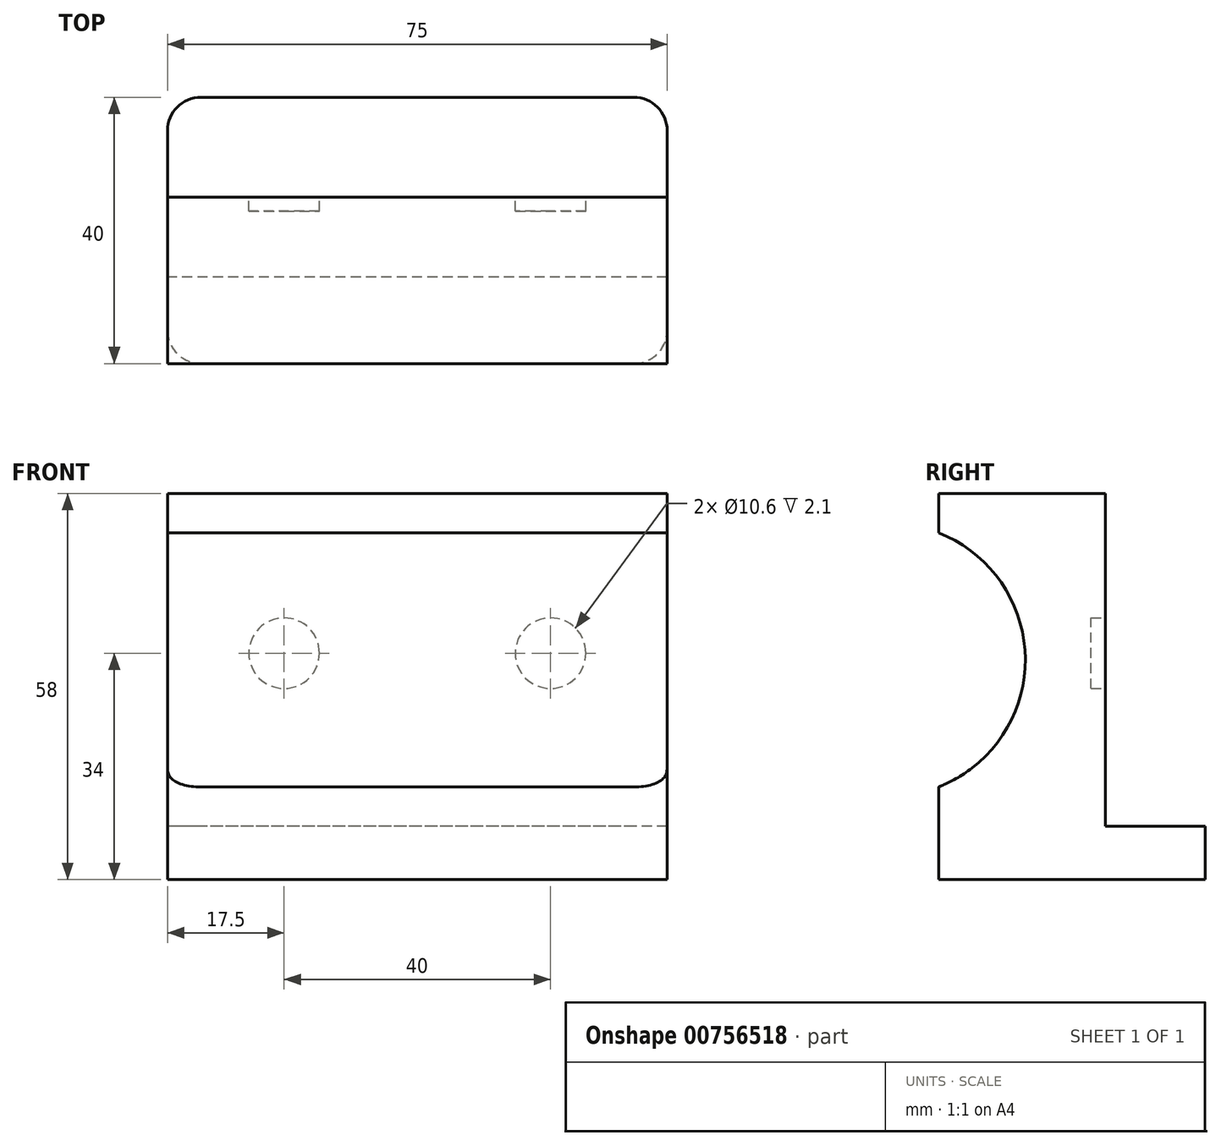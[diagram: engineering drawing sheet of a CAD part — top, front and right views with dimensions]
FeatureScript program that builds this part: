
annotation { "Feature Type Name" : "Feature", "Feature Type Description" : "" }
export const myFeature = defineFeature(function(context is Context, id is Id, definition is map)
    precondition{}
    {
        {
            var Q0;
            Q0=qCreatedBy(makeId("Top.planeOp"),FACE);
            var sketch = newSketch(context, id + "F0", { "sketchPlane" : qUnion([Q0])});
            skLineSegment(sketch, "E0.bottom", {"start": v(37.5, -12.5) * mm, "end": v(-37.5, -12.5) * mm});
            skLineSegment(sketch, "E0.top", {"start": v(37.5, 12.5) * mm, "end": v(-37.5, 12.5) * mm});
            skLineSegment(sketch, "E0.left", {"start": v(37.5, -12.5) * mm, "end": v(37.5, 12.5) * mm});
            skLineSegment(sketch, "E0.right", {"start": v(-37.5, -12.5) * mm, "end": v(-37.5, 12.5) * mm});
            skPoint(sketch, "E0.middle", {"position": v(0, 0) * mm});
            skSolve(sketch);
        }
        {
            var Q0;
            Q0 = qSketchRegion(id + "F0", true);
            extrude(context, id + "F1", {"entities" : qUnion([Q0]), "depth" : 50 * mm, "offsetDistance" : 25 * mm});
        }
        {
            var Q0;
            Q0=qCreatedBy(makeId("Right.planeOp"),FACE);
            var sketch = newSketch(context, id + "F2", { "sketchPlane" : qUnion([Q0])});
            skLineSegment(sketch, "E1", {"start": v(0, 0) * mm, "end": v(-20, 0) * mm});
            skLineSegment(sketch, "E2", {"start": v(-20, 0) * mm, "end": v(-20, 25) * mm});
            skCircle(sketch, "E3", {"center": v(-20, 25) * mm, "radius": 20.5 * mm});
            skSolve(sketch);
        }
        {
            var Q0;
            Q0 = qSketchRegion(id + "F2", true);
            extrude(context, id + "F3", {"entities" : qUnion([Q0]), "endBound" : BoundingType.SYMMETRIC, "depth" : 100 * mm, "offsetDistance" : 25 * mm});
        }
        {
            var Q0;
            Q0=makeQuery(id+"F3.opExtrude","SWEPT_BODY",BODY,{"disambiguationData":[OSD([sQuery(id+"F2.wireOp",EDGE,"E3")])]});
            var Q1;
            Q1=makeQuery(id+"F1.opExtrude","SWEPT_BODY",BODY,{"disambiguationData":[OSD([sQuery(id+"F0.wireOp",EDGE,"E0.bottom"),sQuery(id+"F0.wireOp",EDGE,"E0.top"),sQuery(id+"F0.wireOp",EDGE,"E0.left"),sQuery(id+"F0.wireOp",EDGE,"E0.right")])]});
            booleanBodies(context, id + "F4", {"operationType" : BooleanOperationType.SUBTRACTION, "tools" : qUnion([Q0]), "targets" : qUnion([Q1])});
        }
        {
            var Q0;
            Q0=qCreatedBy(makeId("Top.planeOp"),FACE);
            var sketch = newSketch(context, id + "F5", { "sketchPlane" : qUnion([Q0])});
            skLineSegment(sketch, "E4.bottom", {"start": v(37.5, -20) * mm, "end": v(-37.5, -20) * mm});
            skLineSegment(sketch, "E4.top", {"start": v(37.5, 20) * mm, "end": v(-37.5, 20) * mm});
            skLineSegment(sketch, "E4.left", {"start": v(37.5, -20) * mm, "end": v(37.5, 20) * mm});
            skLineSegment(sketch, "E4.right", {"start": v(-37.5, -20) * mm, "end": v(-37.5, 20) * mm});
            skPoint(sketch, "E4.middle", {"position": v(0, 0) * mm});
            skSolve(sketch);
        }
        {
            var Q0;
            Q0 = qSketchRegion(id + "F5", true);
            extrude(context, id + "F6", {"entities" : qUnion([Q0]), "depth" : 8 * mm, "offsetDistance" : 25 * mm});
        }
        {
            var Q0;
            Q0=makeQuery(id+"F6.opExtrude","SWEPT_BODY",BODY,{"disambiguationData":[OSD([sQuery(id+"F5.wireOp",EDGE,"E4.bottom"),sQuery(id+"F5.wireOp",EDGE,"E4.top"),sQuery(id+"F5.wireOp",EDGE,"E4.left"),sQuery(id+"F5.wireOp",EDGE,"E4.right")])]});
            transform(context, id + "F7", {"entities" : qUnion([Q0]), "transformType" : TransformType.TRANSLATION_3D, "dx" : 0 * mm, "dy" : 7.5 * mm, "dz" : -8 * mm, "makeCopy" : false});
        }
        {
            var Q0;
            Q0=makeQuery(id+"F6.opExtrude","SWEPT_BODY",BODY,{"disambiguationData":[OSD([sQuery(id+"F5.wireOp",EDGE,"E4.bottom"),sQuery(id+"F5.wireOp",EDGE,"E4.top"),sQuery(id+"F5.wireOp",EDGE,"E4.left"),sQuery(id+"F5.wireOp",EDGE,"E4.right")])]});
            var Q1;
            Q1=makeQuery(id+"F1.opExtrude","SWEPT_BODY",BODY,{"disambiguationData":[OSD([sQuery(id+"F0.wireOp",EDGE,"E0.bottom"),sQuery(id+"F0.wireOp",EDGE,"E0.top"),sQuery(id+"F0.wireOp",EDGE,"E0.left"),sQuery(id+"F0.wireOp",EDGE,"E0.right")])]});
            booleanBodies(context, id + "F8", {"operationType" : BooleanOperationType.UNION, "tools" : qUnion([Q0, Q1])});
        }
        {
            var Q0;
            {var subQ0=sQuery(id+"F0.wireOp",EDGE,"E0.bottom");var subQ1=sQuery(id+"F0.wireOp",EDGE,"E0.left");Q0=makeQuery(id+"F8.opBoolean","MERGE",EDGE,{"derivedFrom":[makeQuery(id+"F4.opBoolean","SPLIT",EDGE,{"disambiguationData":[TD([makeQuery(id+"F1.opExtrude","CAP_FACE",FACE,{"disambiguationData":[OSD([subQ0,sQuery(id+"F0.wireOp",EDGE,"E0.top"),subQ1,sQuery(id+"F0.wireOp",EDGE,"E0.right")])],"isStart":true})])],"derivedFrom":makeQuery(id+"F1.opExtrude","SWEPT_EDGE",EDGE,{"disambiguationData":[OSD([subQ0,subQ1])]})}),makeQuery(id+"F6.opExtrude","SWEPT_EDGE",EDGE,{"disambiguationData":[OSD([sQuery(id+"F5.wireOp",EDGE,"E4.bottom"),sQuery(id+"F5.wireOp",EDGE,"E4.left")])]})]});}
            var Q1;
            {var subQ0=sQuery(id+"F0.wireOp",EDGE,"E0.bottom");var subQ1=sQuery(id+"F0.wireOp",EDGE,"E0.right");Q1=makeQuery(id+"F8.opBoolean","MERGE",EDGE,{"derivedFrom":[makeQuery(id+"F4.opBoolean","SPLIT",EDGE,{"disambiguationData":[TD([makeQuery(id+"F1.opExtrude","CAP_FACE",FACE,{"disambiguationData":[OSD([subQ0,sQuery(id+"F0.wireOp",EDGE,"E0.top"),sQuery(id+"F0.wireOp",EDGE,"E0.left"),subQ1])],"isStart":true})])],"derivedFrom":makeQuery(id+"F1.opExtrude","SWEPT_EDGE",EDGE,{"disambiguationData":[OSD([subQ0,subQ1])]})}),makeQuery(id+"F6.opExtrude","SWEPT_EDGE",EDGE,{"disambiguationData":[OSD([sQuery(id+"F5.wireOp",EDGE,"E4.bottom"),sQuery(id+"F5.wireOp",EDGE,"E4.right")])]})]});}
            var Q2;
            Q2=makeQuery(id+"F6.opExtrude","SWEPT_EDGE",EDGE,{"disambiguationData":[OSD([sQuery(id+"F5.wireOp",EDGE,"E4.top"),sQuery(id+"F5.wireOp",EDGE,"E4.left")])]});
            var Q3;
            Q3=makeQuery(id+"F6.opExtrude","SWEPT_EDGE",EDGE,{"disambiguationData":[OSD([sQuery(id+"F5.wireOp",EDGE,"E4.top"),sQuery(id+"F5.wireOp",EDGE,"E4.right")])]});
            fillet(context, id + "F9", {"entities" : qUnion([Q0, Q1, Q2, Q3]), "radius" : 5 * mm, "tangentPropagation" : true, "allowEdgeOverflow" : false});
        }
        {
            var Q0;
            Q0=qCreatedBy(makeId("Front.planeOp"),FACE);
            var sketch = newSketch(context, id + "F10", { "sketchPlane" : qUnion([Q0])});
            skLineSegment(sketch, "E5", {"start": v(0, 0) * mm, "end": v(0, 26) * mm});
            skLineSegment(sketch, "E6", {"start": v(0, 26) * mm, "end": v(-20, 26) * mm});
            skCircle(sketch, "E7", {"center": v(-20, 26) * mm, "radius": 5.3 * mm});
            skSolve(sketch);
        }
        {
            var Q0;
            Q0 = qSketchRegion(id + "F10", true);
            extrude(context, id + "F11", {"entities" : qUnion([Q0]), "depth" : 2.1 * mm, "offsetDistance" : 25 * mm});
        }
        {
            var Q0;
            Q0=makeQuery(id+"F11.opExtrude","SWEPT_BODY",BODY,{"disambiguationData":[OSD([sQuery(id+"F10.wireOp",EDGE,"E7")])]});
            transform(context, id + "F12", {"entities" : qUnion([Q0]), "transformType" : TransformType.TRANSLATION_3D, "dx" : 0 * mm, "dy" : 12.5 * mm, "dz" : 0 * mm, "makeCopy" : false});
        }
        {
            var Q0;
            Q0=makeQuery(id+"F11.opExtrude","SWEPT_BODY",BODY,{"disambiguationData":[OSD([sQuery(id+"F10.wireOp",EDGE,"E7")])]});
            var Q1;
            Q1=qCreatedBy(makeId("Right.planeOp"),FACE);
            mirror(context, id + "F13", {"entities" : qUnion([Q0]), "mirrorPlane" : qUnion([Q1])});
        }
        {
            var Q0;
            Q0=makeQuery(id+"F11.opExtrude","SWEPT_BODY",BODY,{"disambiguationData":[OSD([sQuery(id+"F10.wireOp",EDGE,"E7")])]});
            var Q1;
            Q1=makeQuery(id+"F13.opPattern","COPY",BODY,{"derivedFrom":makeQuery(id+"F11.opExtrude","SWEPT_BODY",BODY,{"disambiguationData":[OSD([sQuery(id+"F10.wireOp",EDGE,"E7")])]}),"instanceName":"1"});
            var Q2;
            Q2=makeQuery(id+"F6.opExtrude","SWEPT_BODY",BODY,{"disambiguationData":[OSD([sQuery(id+"F5.wireOp",EDGE,"E4.bottom"),sQuery(id+"F5.wireOp",EDGE,"E4.top"),sQuery(id+"F5.wireOp",EDGE,"E4.left"),sQuery(id+"F5.wireOp",EDGE,"E4.right")])]});
            booleanBodies(context, id + "F14", {"operationType" : BooleanOperationType.SUBTRACTION, "tools" : qUnion([Q0, Q1]), "targets" : qUnion([Q2])});
        }
    });
